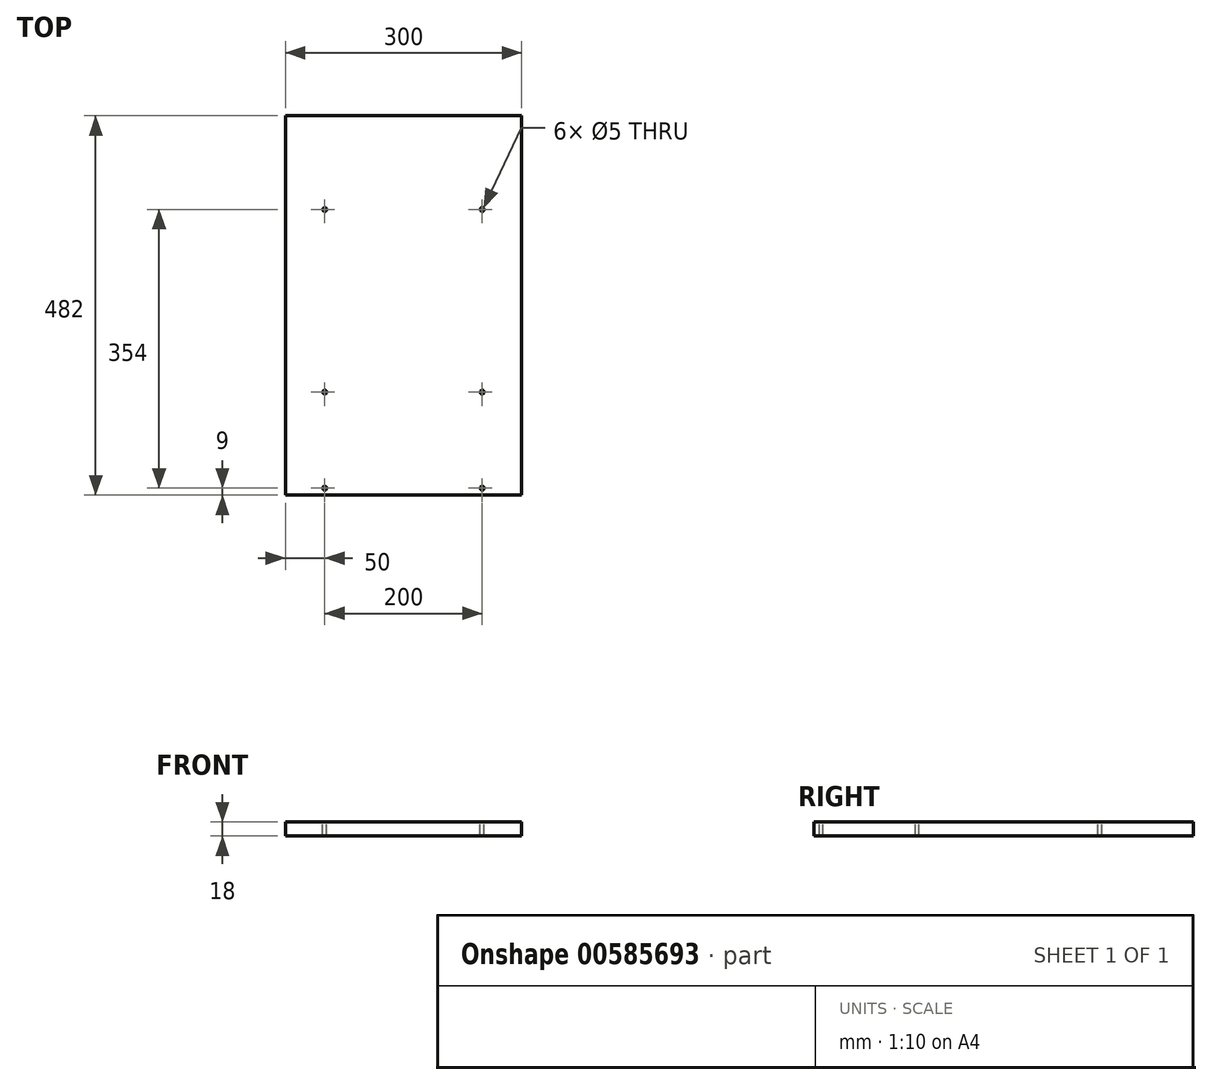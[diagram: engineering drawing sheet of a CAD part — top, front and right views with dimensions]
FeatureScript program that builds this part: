
annotation { "Feature Type Name" : "Feature", "Feature Type Description" : "" }
export const myFeature = defineFeature(function(context is Context, id is Id, definition is map)
    precondition{}
    {
        {
            var Q0;
            Q0=qCreatedBy(makeId("Top.planeOp"),FACE);
            var sketch = newSketch(context, id + "F0", { "sketchPlane" : qUnion([Q0])});
            skLineSegment(sketch, "E0.bottom", {"start": v(0, 0) * mm, "end": v(-300, 0) * mm});
            skLineSegment(sketch, "E0.top", {"start": v(0, -482) * mm, "end": v(-300, -482) * mm});
            skLineSegment(sketch, "E0.left", {"start": v(0, 0) * mm, "end": v(0, -482) * mm});
            skLineSegment(sketch, "E0.right", {"start": v(-300, 0) * mm, "end": v(-300, -482) * mm});
            skSolve(sketch);
        }
        {
            var Q0;
            Q0=makeQuery(id+"F0.imprint","IMPRINT",FACE,{"disambiguationData":[TD([[makeQuery(id+"F0.imprint","IMPRINT",EDGE,{"derivedFrom":sQuery(id+"F0.wireOp",EDGE,"E0.bottom")}),1.0]])]});
            extrude(context, id + "F1", {"entities" : qUnion([Q0]), "depth" : 18 * mm, "offsetDistance" : 25 * mm});
        }
        {
            var Q0;
            Q0=makeQuery(id+"F1.opExtrude","CAP_FACE",FACE,{"disambiguationData":[OSD([sQuery(id+"F0.wireOp",EDGE,"E0.bottom"),sQuery(id+"F0.wireOp",EDGE,"E0.top"),sQuery(id+"F0.wireOp",EDGE,"E0.left"),sQuery(id+"F0.wireOp",EDGE,"E0.right")])],"isStart":false});
            var sketch = newSketch(context, id + "F2", { "sketchPlane" : qUnion([Q0])});
            skCircle(sketch, "E1", {"center": v(-250, -119) * mm, "radius": 2.5 * mm});
            skCircle(sketch, "E2", {"center": v(-50, -119) * mm, "radius": 2.5 * mm});
            skCircle(sketch, "E3", {"center": v(-250, -351) * mm, "radius": 2.5 * mm});
            skCircle(sketch, "E4", {"center": v(-50, -351) * mm, "radius": 2.5 * mm});
            skCircle(sketch, "E5", {"center": v(-250, -473) * mm, "radius": 2.5 * mm});
            skCircle(sketch, "E6", {"center": v(-50, -473) * mm, "radius": 2.5 * mm});
            skSolve(sketch);
        }
        {
            var Q0;
            Q0 = qSketchRegion(id + "F2", true);
            extrude(context, id + "F3", {"entities" : qUnion([Q0]), "operationType" : NewBodyOperationType.REMOVE, "oppositeDirection" : true, "depth" : 18 * mm, "offsetDistance" : 25 * mm});
        }
    });
